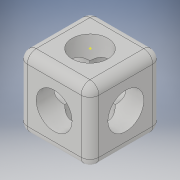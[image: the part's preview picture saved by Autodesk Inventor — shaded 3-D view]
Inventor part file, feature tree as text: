
AUTODESK INVENTOR PART (.ipt)
format: ipt  version: 2018 (Build 220112000, 112)  size: 167,936 bytes
history: native  units: in
note: dims shown in document units (in); Inventor stores cm internally (conversion verified against a paired STEP export)
features: other x3, hole x3, extrude x1, fillet x1, sketch x1
ambient origin geometry x8: Origin, YZ Plane, XZ Plane, XY Plane, X Axis, Y Axis, Z Axis, Center Point
bodies: Solid1 (feature_tree)
feature tree (9):
  extrude  "Extrusion1"  Depth=1.0in
  fillet  "Fillet1"  Radius=1.0in
  other  "Work Point1"
  hole  "Hole1"  [1 undecoded]
  other  "Work Point2"
  hole  "Hole2"  [1 undecoded]
  other  "Work Point3"
  hole  "Hole3"  [1 undecoded]
  sketch  "Sketch1"  dims[d0=1.0in d1=1.0in d2=1.0in d3=0.0in d4=0.125in d5=1.0in d6=1.0in d7=0.5in d8=0.75in d9=0.119in d10=0.25in d11=0.5635in d12=1.0in d13=0.8108in d14=1.0in d15=1.0in d16=0.5in d17=0.75in d18=0.119in d19=0.25in d20=0.5635in d21=1.0in d22=0.8108in d23=1.0in d24=1.0in d25=0.5in d26=0.75in d27=0.119in d28=0.25in d29=0.5635in d30=1.0in d31=0.8108in]
note: 3 required parameter values undecoded (feature->parameter linkage not recoverable at this tier; creation-order binding heuristic only, values carry confidence <= 0.55)
